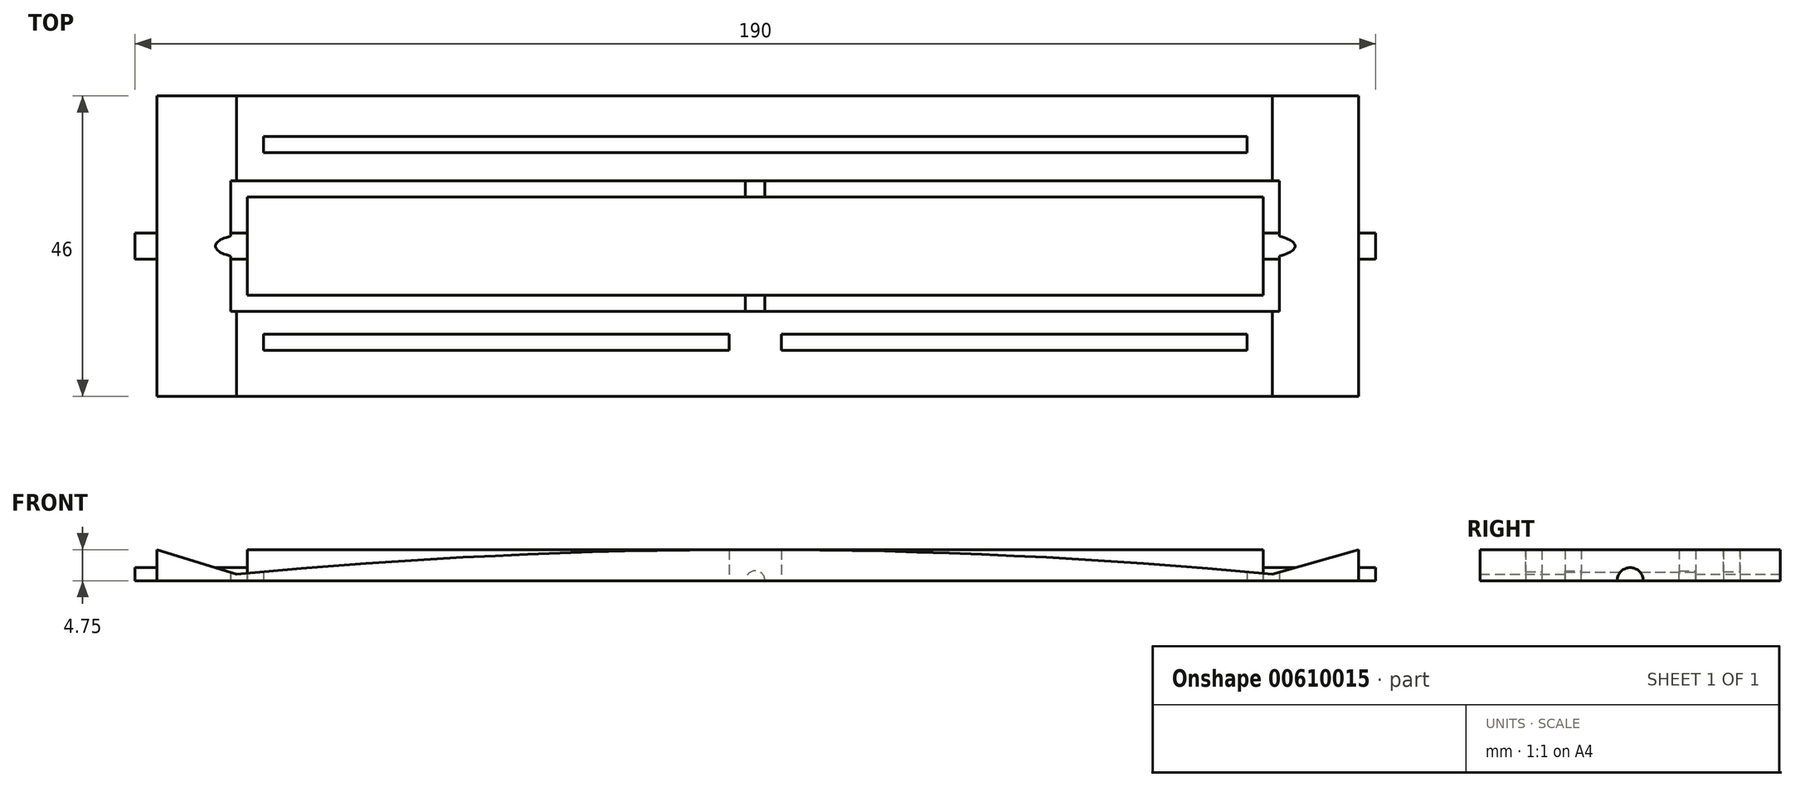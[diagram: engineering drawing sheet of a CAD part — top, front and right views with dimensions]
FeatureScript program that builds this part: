
annotation { "Feature Type Name" : "Feature", "Feature Type Description" : "" }
export const myFeature = defineFeature(function(context is Context, id is Id, definition is map)
    precondition{}
    {
        {
            var Q0;
            Q0=qCreatedBy(makeId("Front.planeOp"),FACE);
            var sketch = newSketch(context, id + "F0", { "sketchPlane" : qUnion([Q0])});
            skPoint(sketch, "E0.middle", {"position": v(0.38, 0) * mm});
            skLineSegment(sketch, "E1", {"start": v(-79.42, 0) * mm, "end": v(79.18, 0) * mm});
            skLineSegment(sketch, "E2.bottom", {"start": v(-79.42, 0) * mm, "end": v(-91.62, 0) * mm});
            skLineSegment(sketch, "E3.bottom", {"start": v(79.18, 0) * mm, "end": v(92.38, 0) * mm});
            skLineSegment(sketch, "E4.bottom", {"start": v(-91.62, 0) * mm, "end": v(92.38, 0) * mm});
            skLineSegment(sketch, "E4.top", {"start": v(-91.62, 4.75) * mm, "end": v(92.38, 4.75) * mm});
            skArc(sketch, "E5", {"start": v(1.5, 0) * mm, "mid": v(0, 1.5) * mm, "end": v(-1.5, 0) * mm});
            skLineSegment(sketch, "E6", {"start": v(-1.5, 0) * mm, "end": v(1.5, 0) * mm});
            skLineSegment(sketch, "E7", {"start": v(0, 0) * mm, "end": v(0, 4.75) * mm});
            skArc(sketch, "E8", {"start": v(79.18, 1) * mm, "mid": v(-0.12, 4.75) * mm, "end": v(-79.42, 1) * mm});
            skLineSegment(sketch, "E9.bottom", {"start": v(92.38, 4.75) * mm, "end": v(-91.62, 4.75) * mm});
            skLineSegment(sketch, "E9.left", {"start": v(92.38, 4.75) * mm, "end": v(92.38, 0) * mm});
            skLineSegment(sketch, "E9.right", {"start": v(-91.62, 4.75) * mm, "end": v(-91.62, 0) * mm});
            skLineSegment(sketch, "E10", {"start": v(79.18, 1) * mm, "end": v(92.38, 4.75) * mm});
            skLineSegment(sketch, "E11", {"start": v(-79.42, 1) * mm, "end": v(-91.62, 4.75) * mm});
            skPoint(sketch, "E12.orphan", {"position": v(92.38, -4.75) * mm});
            skPoint(sketch, "E13.orphan", {"position": v(-91.62, -4.75) * mm});
            skSolve(sketch);
        }
        {
            var Q0;
            Q0=qCreatedBy(makeId("Front.planeOp"),FACE);
            var sketch = newSketch(context, id + "F1", { "sketchPlane" : qUnion([Q0])});
            skLineSegment(sketch, "E14.bottom", {"start": v(0, 0) * mm, "end": v(-87.5, 0) * mm});
            skLineSegment(sketch, "E14.top", {"start": v(0, 4.7) * mm, "end": v(-87.5, 4.7) * mm});
            skLineSegment(sketch, "E14.left", {"start": v(0, 0) * mm, "end": v(0, 4.7) * mm});
            skLineSegment(sketch, "E14.right", {"start": v(-87.5, 0) * mm, "end": v(-87.5, 4.7) * mm});
            skLineSegment(sketch, "E15.bottom", {"start": v(0, 0) * mm, "end": v(87.5, 0) * mm});
            skLineSegment(sketch, "E15.top", {"start": v(0, 4.7) * mm, "end": v(87.5, 4.7) * mm});
            skLineSegment(sketch, "E15.right", {"start": v(87.5, 0) * mm, "end": v(87.5, 4.7) * mm});
            skSolve(sketch);
        }
        {
            var Q0;
            Q0=qCreatedBy(makeId("Top.planeOp"),FACE);
            var sketch = newSketch(context, id + "F2", { "sketchPlane" : qUnion([Q0])});
            skPoint(sketch, "E16.middle", {"position": v(0, 0) * mm});
            skLineSegment(sketch, "E17.right", {"start": v(75.3, 16.8) * mm, "end": v(75.3, 14.3) * mm});
            skLineSegment(sketch, "E18.right", {"start": v(75.3, -13.5) * mm, "end": v(75.3, -16) * mm});
            skLineSegment(sketch, "E19.right", {"start": v(4, -13.5) * mm, "end": v(4, -16) * mm});
            skLineSegment(sketch, "E20.right", {"start": v(-4, -13.5) * mm, "end": v(-4, -16) * mm});
            skLineSegment(sketch, "E21.right", {"start": v(-75.3, -13.5) * mm, "end": v(-75.3, -16) * mm});
            skLineSegment(sketch, "E22.right", {"start": v(-75.3, 16.8) * mm, "end": v(-75.3, 14.3) * mm});
            skLineSegment(sketch, "E23", {"start": v(4, -13.5) * mm, "end": v(75.3, -13.5) * mm});
            skLineSegment(sketch, "E24", {"start": v(75.3, -16) * mm, "end": v(4, -16) * mm});
            skLineSegment(sketch, "E25", {"start": v(-75.3, -16) * mm, "end": v(-4, -16) * mm});
            skLineSegment(sketch, "E26", {"start": v(-4, -13.5) * mm, "end": v(-75.3, -13.5) * mm});
            skLineSegment(sketch, "E27", {"start": v(-75.3, 14.3) * mm, "end": v(75.3, 14.3) * mm});
            skLineSegment(sketch, "E28", {"start": v(75.3, 16.8) * mm, "end": v(-75.3, 16.8) * mm});
            skLineSegment(sketch, "E29.bottom", {"start": v(-80.3, 10) * mm, "end": v(80.3, 10) * mm});
            skLineSegment(sketch, "E29.top", {"start": v(-80.3, -10) * mm, "end": v(80.3, -10) * mm});
            skLineSegment(sketch, "E29.left", {"start": v(-80.3, 10) * mm, "end": v(-80.3, -10) * mm});
            skLineSegment(sketch, "E29.right", {"start": v(80.3, 10) * mm, "end": v(80.3, -10) * mm});
            skLineSegment(sketch, "E30.0", {"start": v(-77.8, 7.5) * mm, "end": v(77.8, 7.5) * mm});
            skLineSegment(sketch, "E30.1", {"start": v(-77.8, 7.5) * mm, "end": v(-77.8, -7.5) * mm});
            skLineSegment(sketch, "E30.2", {"start": v(-77.8, -7.5) * mm, "end": v(77.8, -7.5) * mm});
            skLineSegment(sketch, "E30.3", {"start": v(77.8, 7.5) * mm, "end": v(77.8, -7.5) * mm});
            skLineSegment(sketch, "E31.bottom", {"start": v(-97.5, 27.5) * mm, "end": v(97.5, 27.5) * mm});
            skLineSegment(sketch, "E31.top", {"start": v(-97.5, -27.5) * mm, "end": v(97.5, -27.5) * mm});
            skLineSegment(sketch, "E31.left", {"start": v(-97.5, 27.5) * mm, "end": v(-97.5, -27.5) * mm});
            skLineSegment(sketch, "E31.right", {"start": v(97.5, 27.5) * mm, "end": v(97.5, -27.5) * mm});
            skLineSegment(sketch, "E32.bottom", {"start": v(-92.5, 23.5) * mm, "end": v(92.5, 23.5) * mm});
            skLineSegment(sketch, "E32.top", {"start": v(-92.5, -23.5) * mm, "end": v(92.5, -23.5) * mm});
            skLineSegment(sketch, "E32.left", {"start": v(-91.5, 23.5) * mm, "end": v(-91.5, -23.5) * mm});
            skLineSegment(sketch, "E32.right", {"start": v(92.5, 23.5) * mm, "end": v(92.5, -23.5) * mm});
            skLineSegment(sketch, "E33.0", {"start": v(-94.5, 25.5) * mm, "end": v(94.5, 25.5) * mm});
            skLineSegment(sketch, "E33.1", {"start": v(-93.5, 25.5) * mm, "end": v(-93.5, -25.5) * mm});
            skLineSegment(sketch, "E33.2", {"start": v(-94.5, -25.5) * mm, "end": v(94.5, -25.5) * mm});
            skLineSegment(sketch, "E33.3", {"start": v(94.5, 25.5) * mm, "end": v(94.5, -25.5) * mm});
            skSolve(sketch);
        }
        {
            var Q0;
            {var subQ1=sQuery(id+"F0.wireOp",EDGE,"ys3EQ4KL-TVGB-806q-ErAp-uFSxgdwoMIFN");Q0=makeQuery(id+"F0.imprint","IMPRINT",FACE,{"disambiguationData":[TD([[makeQuery(id+"F0.imprint","IMPRINT",EDGE,{"derivedFrom":subQ1}),1.0]])]});}
            var Q1;
            Q1=makeQuery(id+"F0.imprint","IMPRINT",FACE,{"disambiguationData":[TD([[makeQuery(id+"F0.imprint","IMPRINT",EDGE,{"derivedFrom":sQuery(id+"F0.wireOp",EDGE,"2Xmcz634-q65L-OcEz-RFky-VBpyImEll2yt.bottom")}),-1.0]])]});
            var Q2;
            Q2=makeQuery(id+"F0.imprint","IMPRINT",FACE,{"disambiguationData":[TD([[makeQuery(id+"F0.imprint","IMPRINT",EDGE,{"derivedFrom":sQuery(id+"F0.wireOp",EDGE,"E5")}),1.0]])]});
            var Q3;
            {var subQ7=sQuery(id+"F0.wireOp",EDGE,"CYJWQcW4-jkQO-EFny-5skn-M0ueQvAqL0zQ");Q3=makeQuery(id+"F0.imprint","IMPRINT",FACE,{"disambiguationData":[TD([[makeQuery(id+"F0.imprint","IMPRINT",EDGE,{"derivedFrom":subQ7}),-1.0]])]});}
            var Q4;
            {var subQ10=sQuery(id+"F0.wireOp",EDGE,"E9.right");Q4=makeQuery(id+"F0.imprint","IMPRINT",FACE,{"disambiguationData":[TD([[makeQuery(id+"F0.imprint","IMPRINT",EDGE,{"derivedFrom":subQ10}),1.0]])]});}
            var Q5;
            {var subQ8=sQuery(id+"F0.wireOp",EDGE,"E9.left");Q5=makeQuery(id+"F0.imprint","IMPRINT",FACE,{"disambiguationData":[TD([[makeQuery(id+"F0.imprint","IMPRINT",EDGE,{"derivedFrom":subQ8}),-1.0]])]});}
            extrude(context, id + "F3", {"entities" : qUnion([Q0, Q1, Q2, Q3, Q4, Q5]), "depth" : 23 * mm, "offsetDistance" : 25 * mm, "hasSecondDirection" : true, "secondDirectionOppositeDirection" : true, "secondDirectionDepth" : 23 * mm});
        }
        {
            var Q0;
            Q0=makeQuery(id+"F2.imprint","IMPRINT",FACE,{"disambiguationData":[TD([[makeQuery(id+"F2.imprint","IMPRINT",EDGE,{"derivedFrom":sQuery(id+"F2.wireOp",EDGE,"E20.right")}),-1.0]])]});
            var Q1;
            Q1=makeQuery(id+"F2.imprint","IMPRINT",FACE,{"disambiguationData":[TD([[makeQuery(id+"F2.imprint","IMPRINT",EDGE,{"derivedFrom":sQuery(id+"F2.wireOp",EDGE,"E18.right")}),-1.0]])]});
            var Q2;
            Q2=makeQuery(id+"F2.imprint","IMPRINT",FACE,{"disambiguationData":[TD([[makeQuery(id+"F2.imprint","IMPRINT",EDGE,{"derivedFrom":sQuery(id+"F2.wireOp",EDGE,"E29.bottom")}),-1.0]])]});
            var Q3;
            Q3=makeQuery(id+"F2.imprint","IMPRINT",FACE,{"disambiguationData":[TD([[makeQuery(id+"F2.imprint","IMPRINT",EDGE,{"derivedFrom":sQuery(id+"F2.wireOp",EDGE,"E17.right")}),-1.0]])]});
            extrude(context, id + "F4", {"entities" : qUnion([Q0, Q1, Q2, Q3]), "operationType" : NewBodyOperationType.REMOVE, "depth" : 5 * mm, "offsetDistance" : 25 * mm});
        }
        {
            var Q0;
            {var subQ4=sQuery(id+"F0.wireOp",EDGE,"E4.left");var subQ5=sQuery(id+"F0.wireOp",EDGE,"E4.top");Q0=makeQuery(id+"Fq9LVFcyxVJ9S5i_1.boolean.opBoolean","SPLIT",FACE,{"disambiguationData":[TD([makeQuery(id+"F3.opExtrude","SWEPT_FACE",FACE,{"disambiguationData":[OSD([subQ4])]})])],"derivedFrom":makeQuery(id+"F3.opExtrude","SWEPT_FACE",FACE,{"disambiguationData":[OSD([subQ5])]})});}
            var sketch = newSketch(context, id + "F5", { "sketchPlane" : qUnion([Q0])});
            skLineSegment(sketch, "E34.bottom", {"start": v(-80.3, 10) * mm, "end": v(-82.3, 10) * mm});
            skLineSegment(sketch, "E34.top", {"start": v(-80.3, -10) * mm, "end": v(-82.3, -10) * mm});
            skLineSegment(sketch, "E34.left", {"start": v(-80.3, 10) * mm, "end": v(-80.3, -10) * mm});
            skLineSegment(sketch, "E34.right", {"start": v(-82.3, 10) * mm, "end": v(-82.3, -10) * mm});
            skLineSegment(sketch, "E35.bottom", {"start": v(80.3, 10) * mm, "end": v(82.3, 10) * mm});
            skLineSegment(sketch, "E35.top", {"start": v(80.3, -10) * mm, "end": v(82.3, -10) * mm});
            skLineSegment(sketch, "E35.left", {"start": v(80.3, 10) * mm, "end": v(80.3, -10) * mm});
            skLineSegment(sketch, "E35.right", {"start": v(82.3, 10) * mm, "end": v(82.3, -10) * mm});
            skSolve(sketch);
        }
        {
            var Q0;
            Q0=qCreatedBy(makeId("Right.planeOp"),FACE);
            var sketch = newSketch(context, id + "F6", { "sketchPlane" : qUnion([Q0])});
            skArc(sketch, "E36", {"start": v(2, 0) * mm, "mid": v(0, 2) * mm, "end": v(-2, 0) * mm});
            skLineSegment(sketch, "E37", {"start": v(-2, 0) * mm, "end": v(2, 0) * mm});
            skSolve(sketch);
        }
        {
            var Q0;
            Q0=qSketchRegion(id+"F6",true);
            extrude(context, id + "F7", {"entities" : qUnion([Q0]), "operationType" : NewBodyOperationType.ADD, "depth" : 95 * mm, "offsetDistance" : 25 * mm, "hasSecondDirection" : true, "secondDirectionOppositeDirection" : true, "secondDirectionDepth" : 95 * mm});
        }
        {
            var Q0;
            Q0=makeQuery(id+"F0.imprint","IMPRINT",FACE,{"disambiguationData":[TD([[makeQuery(id+"F0.imprint","IMPRINT",EDGE,{"derivedFrom":sQuery(id+"F0.wireOp",EDGE,"E5")}),1.0]])]});
            extrude(context, id + "F8", {"entities" : qUnion([Q0]), "operationType" : NewBodyOperationType.ADD, "depth" : 12 * mm, "offsetDistance" : 25 * mm, "hasSecondDirection" : true, "secondDirectionOppositeDirection" : true, "secondDirectionDepth" : 12 * mm});
        }
        {
            var Q0;
            Q0=makeQuery(id+"F2.imprint","IMPRINT",FACE,{"disambiguationData":[TD([[makeQuery(id+"F2.imprint","IMPRINT",EDGE,{"derivedFrom":sQuery(id+"F2.wireOp",EDGE,"E30.0")}),-1.0]])]});
            extrude(context, id + "F9", {"entities" : qUnion([Q0]), "operationType" : NewBodyOperationType.ADD, "depth" : 4.75 * mm, "offsetDistance" : 25 * mm});
        }
    });
